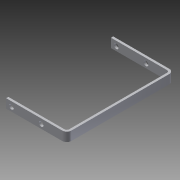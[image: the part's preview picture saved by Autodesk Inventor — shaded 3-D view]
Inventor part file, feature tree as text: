
AUTODESK INVENTOR PART (.ipt)
format: ipt  version: 2013 (Build 170138000, 138)  size: 117,248 bytes
history: native  units: in
note: dims shown in document units (in); Inventor stores cm internally (conversion verified against a paired STEP export)
features: sheet_metal_op x7, other x3, sketch x3, reference x2, extrude x1
ambient origin geometry x8: Origin, YZ Plane, XZ Plane, XY Plane, X Axis, Y Axis, Z Axis, Center Point
feature tree (16):
  sheet_metal_op  "Face2"
  sheet_metal_op  "Flange4"
  sheet_metal_op  "Flange5"
  extrude  "Extrusion2"  Depth=0.5in
  other  "Plate5"
  sketch  "Sketch6"  dims[d1=3.119in d2=0.5in]
  other  "Plate6"
  sheet_metal_op  "Bend4"
  sheet_metal_op  "Corner4"
  sketch  "Sketch7"  dims[d5=0.295in]
  other  "Plate7"
  sheet_metal_op  "Bend5"
  sheet_metal_op  "Corner5"
  sketch  "Sketch8"  dims[d8=0.125in d42=0.125in d43=0.125in d44=0.0625in d45=0.25in d46=0.125in d47=5.697in d48=90.0deg d49=0.125in d50=0.5in d51=0.125in d52=0.125in d53=0.125in d54=0.0625in d55=0.25in d56=0.125in d57=3.369in d58=90.0deg d59=0.125in d60=0.5in d61=0.125in d62=0.125in d63=99999.0in d64=0.0in]
  reference  "Reference1"
  reference  "Reference2"
